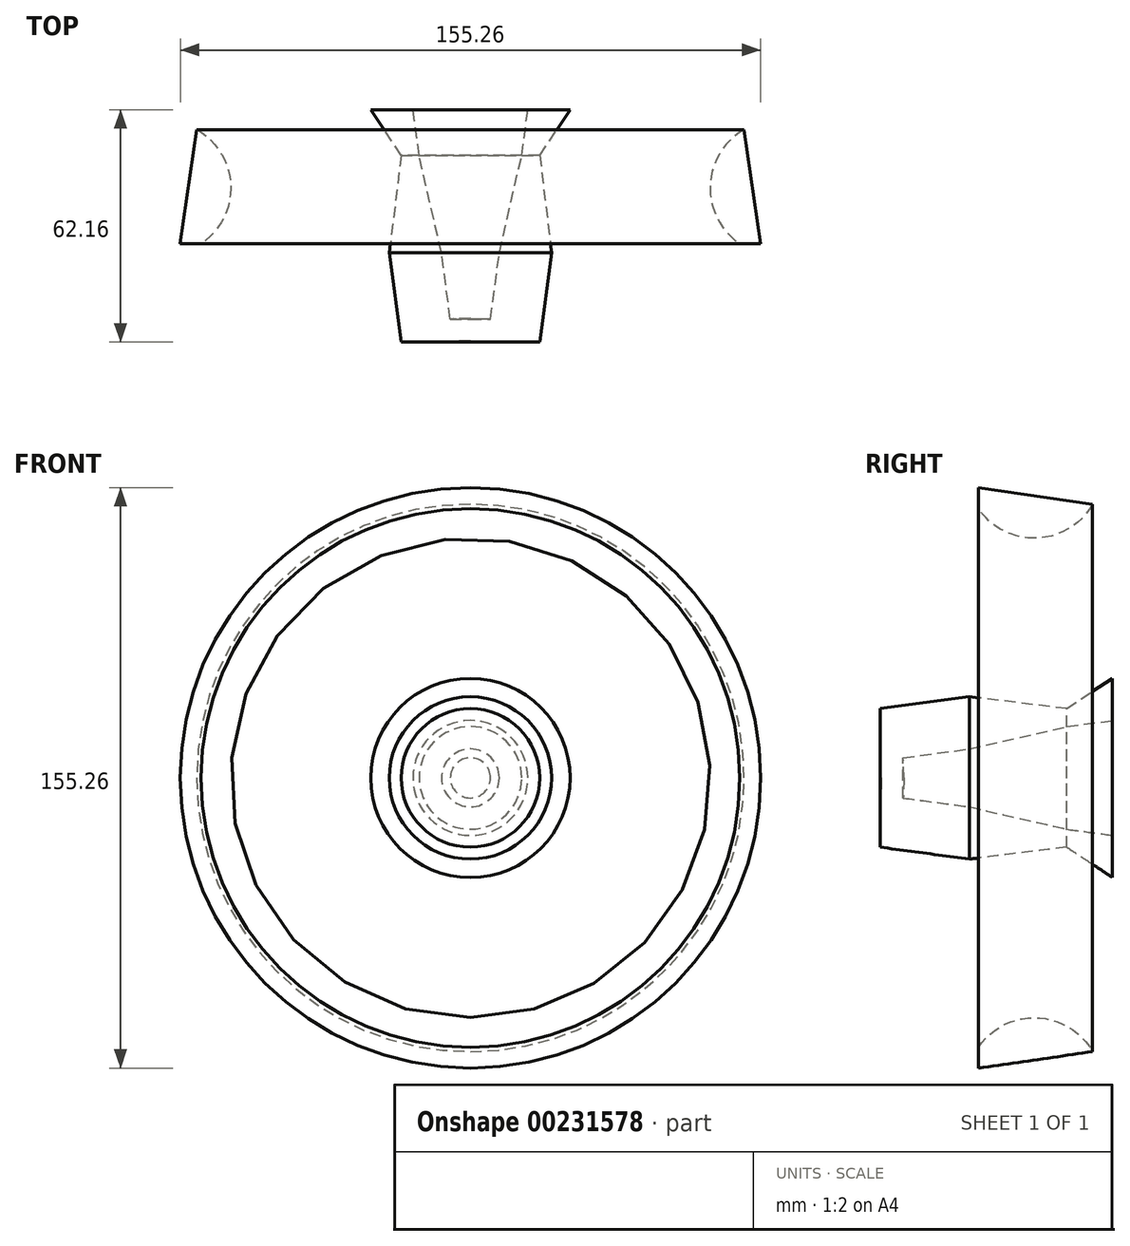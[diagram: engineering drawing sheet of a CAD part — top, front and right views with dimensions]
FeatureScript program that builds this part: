
annotation { "Feature Type Name" : "Feature", "Feature Type Description" : "" }
export const myFeature = defineFeature(function(context is Context, id is Id, definition is map)
    precondition{}
    {
        {
            var Q0;
            Q0=qCreatedBy(makeId("Top.planeOp"),FACE);
            var sketch = newSketch(context, id + "F0", { "sketchPlane" : qUnion([Q0])});
            skLineSegment(sketch, "E0", {"start": v(22.38, 44.68) * mm, "end": v(33.67, 44.68) * mm});
            skLineSegment(sketch, "E1", {"start": v(33.67, 44.68) * mm, "end": v(25.55, 32.45) * mm});
            skLineSegment(sketch, "E2", {"start": v(25.55, 32.45) * mm, "end": v(28.74, 6.38) * mm});
            skLineSegment(sketch, "E3", {"start": v(28.74, 6.38) * mm, "end": v(25.55, -17.48) * mm});
            skLineSegment(sketch, "E4", {"start": v(25.55, -17.48) * mm, "end": v(7.02, -17.24) * mm});
            skLineSegment(sketch, "E5", {"start": v(7.02, -17.24) * mm, "end": v(7.02, -11.12) * mm});
            skLineSegment(sketch, "E6", {"start": v(7.02, -11.12) * mm, "end": v(12.4, -11.32) * mm});
            skLineSegment(sketch, "E7", {"start": v(12.4, -11.32) * mm, "end": v(14.76, 6.38) * mm});
            skLineSegment(sketch, "E8", {"start": v(14.76, 6.38) * mm, "end": v(20.74, 32.45) * mm});
            skLineSegment(sketch, "E9", {"start": v(20.74, 32.45) * mm, "end": v(22.38, 44.68) * mm});
            skLineSegment(sketch, "E10", {"start": v(7.02, -17.24) * mm, "end": v(7.02, 58.22) * mm, "construction": true});
            skArc(sketch, "E11", {"start": v(-65.04, 8.8) * mm, "mid": v(-57.12, 24.4) * mm, "end": v(-66.21, 39.34) * mm});
            skLineSegment(sketch, "E12", {"start": v(-65.04, 8.8) * mm, "end": v(-70.61, 8.8) * mm});
            skLineSegment(sketch, "E13", {"start": v(-70.61, 8.8) * mm, "end": v(-66.21, 39.34) * mm});
            skSolve(sketch);
        }
        {
            var Q0;
            Q0 = qSketchRegion(id + "F0", true);
            var Q1;
            Q1=sQuery(id+"F0.wireOp",EDGE,"E10");
            revolve(context, id + "F1", {"entities" : qUnion([Q0]), "axis" : qUnion([Q1]), "revolveType" : RevolveType.FULL});
        }
    });
